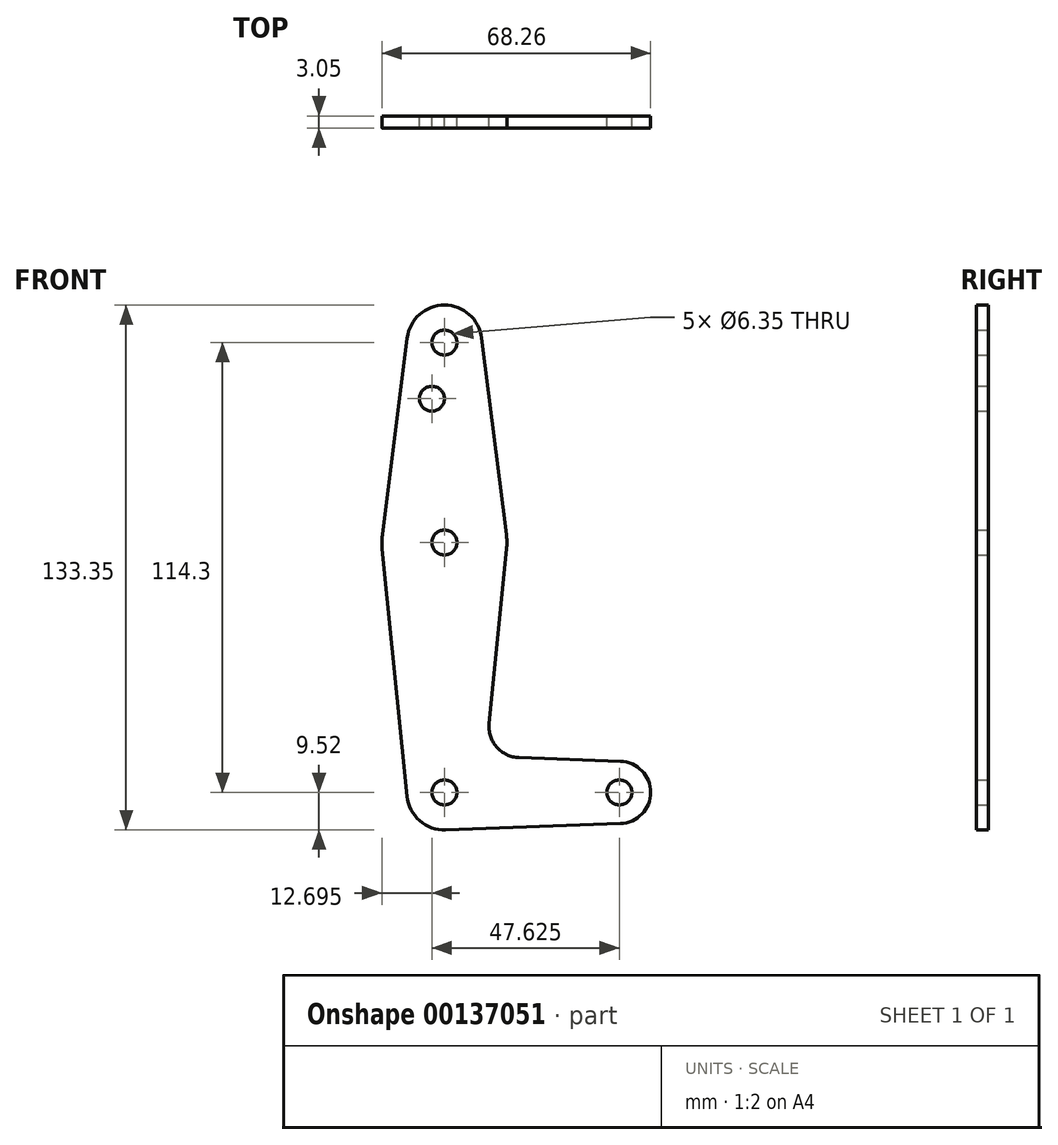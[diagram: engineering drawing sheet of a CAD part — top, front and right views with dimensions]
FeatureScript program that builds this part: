
annotation { "Feature Type Name" : "Feature", "Feature Type Description" : "" }
export const myFeature = defineFeature(function(context is Context, id is Id, definition is map)
    precondition{}
    {
        {
            var Q0;
            Q0=qCreatedBy(makeId("Front.planeOp"),FACE);
            var sketch = newSketch(context, id + "F0", { "sketchPlane" : qUnion([Q0])});
            skLineSegment(sketch, "E0", {"start": v(0, 0) * mm, "end": v(0, 114.3) * mm, "construction": true});
            skLineSegment(sketch, "E1", {"start": v(0, 0) * mm, "end": v(44.45, 0) * mm, "construction": true});
            skCircle(sketch, "E2", {"center": v(44.45, 0) * mm, "radius": 7.94 * mm});
            skCircle(sketch, "E3", {"center": v(0, 0) * mm, "radius": 9.53 * mm});
            skCircle(sketch, "E4", {"center": v(0, 63.5) * mm, "radius": 15.88 * mm});
            skCircle(sketch, "E5", {"center": v(0, 114.3) * mm, "radius": 9.53 * mm});
            skLineSegment(sketch, "E6", {"start": v(-9.45, 115.5) * mm, "end": v(-15.75, 65.48) * mm});
            skLineSegment(sketch, "E7", {"start": v(9.45, 115.5) * mm, "end": v(15.75, 65.48) * mm});
            skLineSegment(sketch, "E8", {"start": v(-15.8, 61.91) * mm, "end": v(-9.48, -0.95) * mm});
            skLineSegment(sketch, "E9", {"start": v(11.34, 17.58) * mm, "end": v(15.8, 61.91) * mm});
            skLineSegment(sketch, "E10", {"start": v(18.95, 8.85) * mm, "end": v(44.73, 7.93) * mm});
            skLineSegment(sketch, "E11", {"start": v(0.34, -9.52) * mm, "end": v(44.73, -7.93) * mm});
            skArc(sketch, "E12.filletArc", {"start": v(11.34, 17.58) * mm, "mid": v(13.26, 11.57) * mm, "end": v(18.95, 8.85) * mm});
            skLineSegment(sketch, "E13", {"start": v(0, 63.5) * mm, "end": v(0, 100.03) * mm, "construction": true});
            skLineSegment(sketch, "E14", {"start": v(0, 100.03) * mm, "end": v(-3.18, 100.03) * mm, "construction": true});
            skCircle(sketch, "E15", {"center": v(0, 114.3) * mm, "radius": 3.18 * mm});
            skCircle(sketch, "E16", {"center": v(-3.18, 100.03) * mm, "radius": 3.18 * mm});
            skCircle(sketch, "E17", {"center": v(0, 63.5) * mm, "radius": 3.18 * mm});
            skCircle(sketch, "E18", {"center": v(0, 0) * mm, "radius": 3.18 * mm});
            skCircle(sketch, "E19", {"center": v(44.45, 0) * mm, "radius": 3.18 * mm});
            skSolve(sketch);
        }
        {
            var Q0;
            Q0=makeQuery(id+"F0.imprint","IMPRINT",FACE,{"disambiguationData":[TD([[makeQuery(id+"F0.imprint","IMPRINT",EDGE,{"derivedFrom":sQuery(id+"F0.wireOp",EDGE,"E15")}),-1.0]])]});
            var Q1;
            {var subQ1=sQuery(id+"F0.wireOp",EDGE,"E6");Q1=makeQuery(id+"F0.imprint","IMPRINT",FACE,{"disambiguationData":[TD([[makeQuery(id+"F0.imprint","IMPRINT",EDGE,{"derivedFrom":subQ1}),1.0]])]});}
            var Q2;
            Q2=makeQuery(id+"F0.imprint","IMPRINT",FACE,{"disambiguationData":[TD([[makeQuery(id+"F0.imprint","IMPRINT",EDGE,{"derivedFrom":sQuery(id+"F0.wireOp",EDGE,"E17")}),-1.0]])]});
            var Q3;
            {var subQ0=sQuery(id+"F0.wireOp",EDGE,"E8");Q3=makeQuery(id+"F0.imprint","IMPRINT",FACE,{"disambiguationData":[TD([[makeQuery(id+"F0.imprint","IMPRINT",EDGE,{"derivedFrom":subQ0}),1.0]])]});}
            var Q4;
            Q4=makeQuery(id+"F0.imprint","IMPRINT",FACE,{"disambiguationData":[TD([[makeQuery(id+"F0.imprint","IMPRINT",EDGE,{"derivedFrom":sQuery(id+"F0.wireOp",EDGE,"E18")}),-1.0]])]});
            var Q5;
            Q5=makeQuery(id+"F0.imprint","IMPRINT",FACE,{"disambiguationData":[TD([[makeQuery(id+"F0.imprint","IMPRINT",EDGE,{"derivedFrom":sQuery(id+"F0.wireOp",EDGE,"E19")}),-1.0]])]});
            extrude(context, id + "F1", {"entities" : qUnion([Q0, Q1, Q2, Q3, Q4, Q5]), "depth" : 3.05 * mm});
        }
    });
